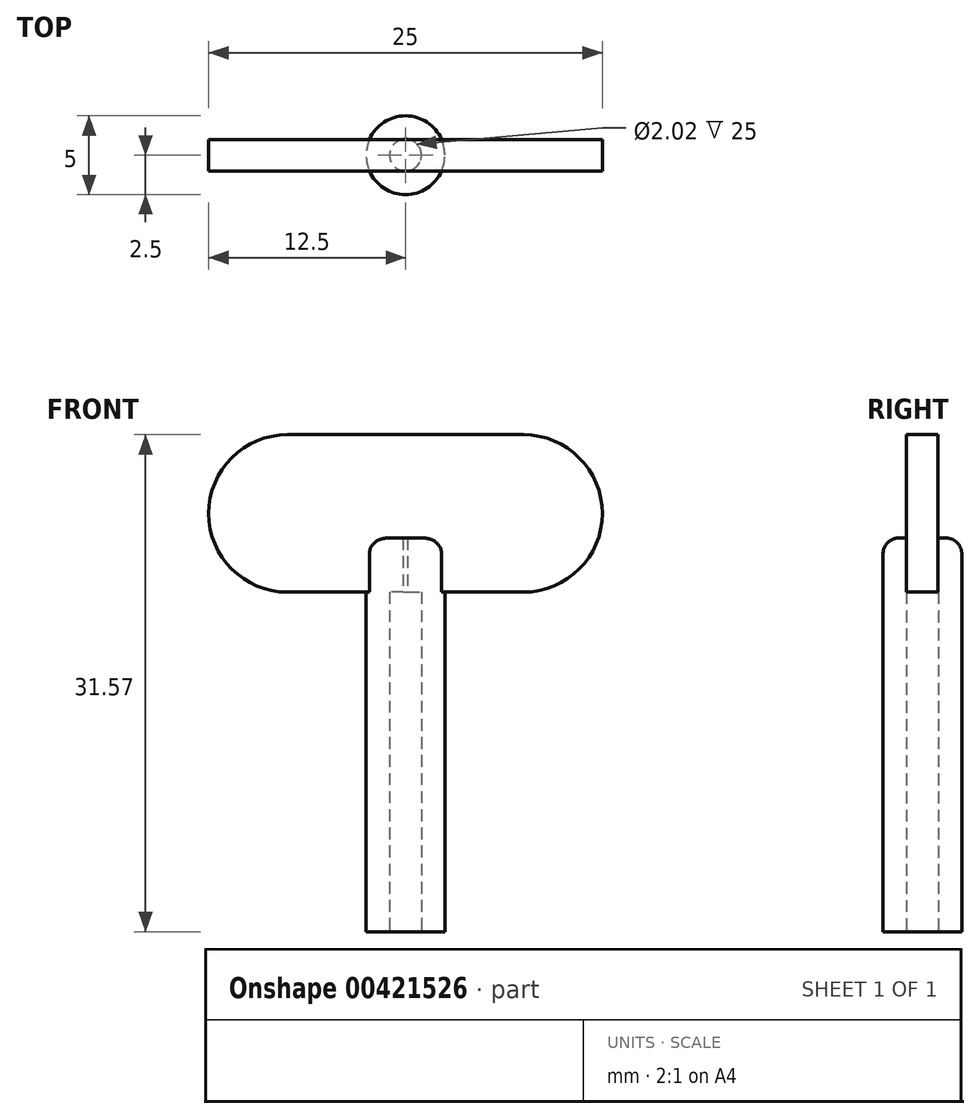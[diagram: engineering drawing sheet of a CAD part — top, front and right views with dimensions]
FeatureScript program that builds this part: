
annotation { "Feature Type Name" : "Feature", "Feature Type Description" : "" }
export const myFeature = defineFeature(function(context is Context, id is Id, definition is map)
    precondition{}
    {
        {
            var Q0;
            Q0=qCreatedBy(makeId("Top.planeOp"),FACE);
            var sketch = newSketch(context, id + "F0", { "sketchPlane" : qUnion([Q0])});
            skCircle(sketch, "E0", {"center": v(0, 0) * mm, "radius": 2.5 * mm});
            skCircle(sketch, "E1", {"center": v(0, 0) * mm, "radius": 1.01 * mm});
            skSolve(sketch);
        }
        {
            var Q0;
            Q0=makeQuery(id+"F0.imprint","IMPRINT",FACE,{"disambiguationData":[TD([[makeQuery(id+"F0.imprint","IMPRINT",EDGE,{"derivedFrom":sQuery(id+"F0.wireOp",EDGE,"E0")}),1.0]])]});
            extrude(context, id + "F1", {"entities" : qUnion([Q0]), "depth" : 25 * mm});
        }
        {
            var Q0;
            Q0=qCreatedBy(makeId("Front.planeOp"),FACE);
            var sketch = newSketch(context, id + "F2", { "sketchPlane" : qUnion([Q0])});
            skLineSegment(sketch, "E2.bottom", {"start": v(-12.5, 21.57) * mm, "end": v(12.5, 21.57) * mm});
            skLineSegment(sketch, "E2.top", {"start": v(-12.5, 31.57) * mm, "end": v(12.5, 31.57) * mm});
            skLineSegment(sketch, "E2.left", {"start": v(-12.5, 21.57) * mm, "end": v(-12.5, 31.57) * mm});
            skLineSegment(sketch, "E2.right", {"start": v(12.5, 21.57) * mm, "end": v(12.5, 31.57) * mm});
            skPoint(sketch, "E2.middle", {"position": v(0, 26.57) * mm});
            skSolve(sketch);
        }
        {
            var Q0;
            Q0=makeQuery(id+"F2.imprint","IMPRINT",FACE,{"disambiguationData":[TD([[makeQuery(id+"F2.imprint","IMPRINT",EDGE,{"derivedFrom":sQuery(id+"F2.wireOp",EDGE,"E2.bottom")}),1.0]])]});
            extrude(context, id + "F3", {"entities" : qUnion([Q0]), "operationType" : NewBodyOperationType.ADD, "depth" : 2 * mm, "symmetric" : true});
        }
        {
            var Q0;
            Q0=makeQuery(id+"F3.opExtrude","SWEPT_EDGE",EDGE,{"disambiguationData":[OSD([sQuery(id+"F2.wireOp",EDGE,"E2.bottom"),sQuery(id+"F2.wireOp",EDGE,"E2.left")])]});
            var Q1;
            Q1=makeQuery(id+"F3.opExtrude","SWEPT_EDGE",EDGE,{"disambiguationData":[OSD([sQuery(id+"F2.wireOp",EDGE,"E2.top"),sQuery(id+"F2.wireOp",EDGE,"E2.left")])]});
            var Q2;
            Q2=makeQuery(id+"F3.opExtrude","SWEPT_EDGE",EDGE,{"disambiguationData":[OSD([sQuery(id+"F2.wireOp",EDGE,"E2.bottom"),sQuery(id+"F2.wireOp",EDGE,"E2.right")])]});
            var Q3;
            Q3=makeQuery(id+"F3.opExtrude","SWEPT_EDGE",EDGE,{"disambiguationData":[OSD([sQuery(id+"F2.wireOp",EDGE,"E2.top"),sQuery(id+"F2.wireOp",EDGE,"E2.right")])]});
            fillet(context, id + "F4", {"entities" : qUnion([Q0, Q1, Q2, Q3]), "radius" : 5 * mm, "tangentPropagation" : true, "allowEdgeOverflow" : false});
        }
        {
            var Q0;
            {var subQ0=sQuery(id+"F0.wireOp",EDGE,"E0");Q0=makeQuery(id+"F3.boolean.opBoolean","SPLIT",EDGE,{"disambiguationData":[TD([makeQuery(id+"F3.opExtrude","CAP_FACE",FACE,{"disambiguationData":[OSD([sQuery(id+"F2.wireOp",EDGE,"E2.bottom"),sQuery(id+"F2.wireOp",EDGE,"E2.top"),sQuery(id+"F2.wireOp",EDGE,"E2.left"),sQuery(id+"F2.wireOp",EDGE,"E2.right")])],"isStart":true})])],"derivedFrom":makeQuery(id+"F1.opExtrude","CAP_EDGE",EDGE,{"disambiguationData":[OSD([subQ0])],"isStart":false})});}
            var Q1;
            {var subQ0=sQuery(id+"F0.wireOp",EDGE,"E0");Q1=makeQuery(id+"F3.boolean.opBoolean","SPLIT",EDGE,{"disambiguationData":[TD([makeQuery(id+"F3.opExtrude","CAP_FACE",FACE,{"disambiguationData":[OSD([sQuery(id+"F2.wireOp",EDGE,"E2.bottom"),sQuery(id+"F2.wireOp",EDGE,"E2.top"),sQuery(id+"F2.wireOp",EDGE,"E2.left"),sQuery(id+"F2.wireOp",EDGE,"E2.right")])],"isStart":false})])],"derivedFrom":makeQuery(id+"F1.opExtrude","CAP_EDGE",EDGE,{"disambiguationData":[OSD([subQ0])],"isStart":false})});}
            fillet(context, id + "F5", {"entities" : qUnion([Q0, Q1]), "radius" : 1 * mm, "allowEdgeOverflow" : false});
        }
    });
